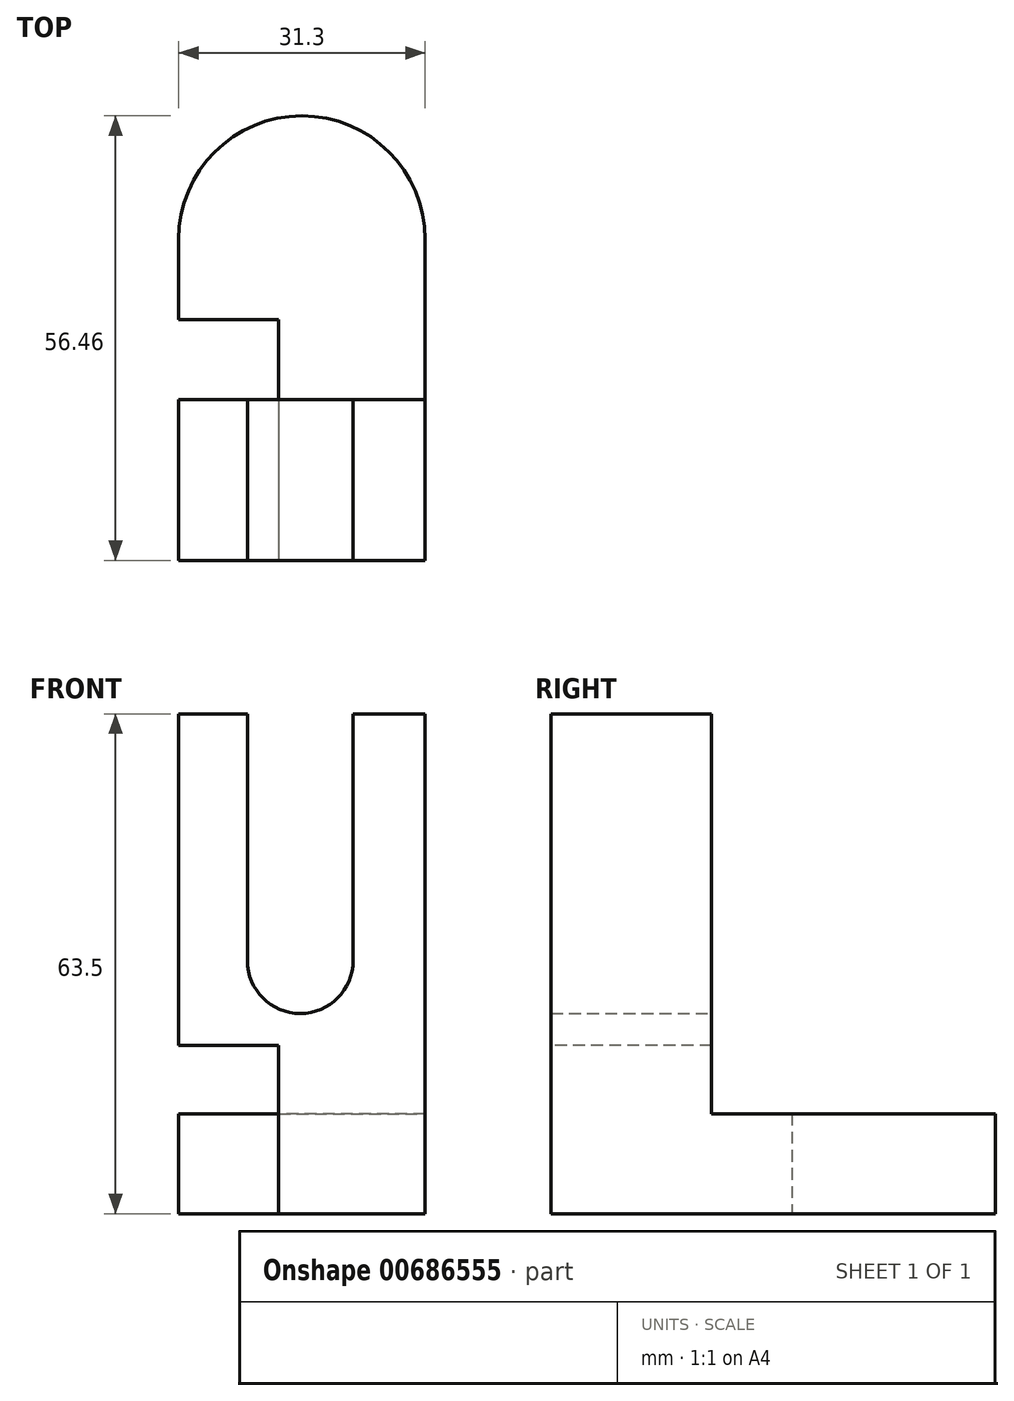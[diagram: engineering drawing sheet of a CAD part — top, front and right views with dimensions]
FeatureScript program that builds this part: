
annotation { "Feature Type Name" : "Feature", "Feature Type Description" : "" }
export const myFeature = defineFeature(function(context is Context, id is Id, definition is map)
    precondition{}
    {
        {
            var Q0;
            Q0=qCreatedBy(makeId("Top.planeOp"),FACE);
            var sketch = newSketch(context, id + "F0", { "sketchPlane" : qUnion([Q0])});
            skLineSegment(sketch, "E0.top", {"start": v(15.65, -20.4) * mm, "end": v(-15.65, -20.4) * mm});
            skLineSegment(sketch, "E0.left", {"start": v(15.65, 20.4) * mm, "end": v(15.65, -20.4) * mm});
            skLineSegment(sketch, "E0.right", {"start": v(-15.65, 20.4) * mm, "end": v(-15.65, -20.4) * mm});
            skPoint(sketch, "E0.middle", {"position": v(0, 0) * mm});
            skArc(sketch, "E1", {"start": v(15.65, 20.4) * mm, "mid": v(0, 36.06) * mm, "end": v(-15.65, 20.4) * mm});
            skSolve(sketch);
        }
        {
            var Q0;
            Q0=makeQuery(id+"F0.imprint","IMPRINT",FACE,{"disambiguationData":[TD([[makeQuery(id+"F0.imprint","IMPRINT",EDGE,{"derivedFrom":sQuery(id+"F0.wireOp",EDGE,"E0.top")}),-1.0]])]});
            extrude(context, id + "F1", {"entities" : qUnion([Q0]), "depth" : 12.7 * mm, "offsetDistance" : 25.4 * mm});
        }
        {
            var Q0;
            Q0=makeQuery(id+"F1.opExtrude","CAP_FACE",FACE,{"disambiguationData":[OSD([sQuery(id+"F0.wireOp",EDGE,"E0.top"),sQuery(id+"F0.wireOp",EDGE,"E0.left"),sQuery(id+"F0.wireOp",EDGE,"E0.right"),sQuery(id+"F0.wireOp",EDGE,"E1")])],"isStart":false});
            var sketch = newSketch(context, id + "F2", { "sketchPlane" : qUnion([Q0])});
            skLineSegment(sketch, "E2", {"start": v(-15.65, 0) * mm, "end": v(15.65, 0) * mm});
            skLineSegment(sketch, "E3", {"start": v(15.65, 0) * mm, "end": v(15.65, -20.4) * mm});
            skLineSegment(sketch, "E4", {"start": v(15.65, -20.4) * mm, "end": v(-15.65, -20.4) * mm});
            skLineSegment(sketch, "E5", {"start": v(-15.65, -20.4) * mm, "end": v(-15.65, 0) * mm});
            skSolve(sketch);
        }
        {
            var Q0;
            Q0=makeQuery(id+"F2.imprint","IMPRINT",FACE,{"disambiguationData":[TD([[makeQuery(id+"F2.imprint","IMPRINT",EDGE,{"derivedFrom":sQuery(id+"F2.wireOp",EDGE,"E2")}),-1.0]])]});
            extrude(context, id + "F3", {"entities" : qUnion([Q0]), "operationType" : NewBodyOperationType.ADD, "depth" : 50.8 * mm, "offsetDistance" : 25.4 * mm});
        }
        {
            var Q0;
            Q0=makeQuery(id+"F3.opExtrude","SWEPT_FACE",FACE,{"disambiguationData":[OSD([sQuery(id+"F2.wireOp",EDGE,"E2")])]});
            var sketch = newSketch(context, id + "F4", { "sketchPlane" : qUnion([Q0])});
            skLineSegment(sketch, "E6.bottom", {"start": v(-6.51, 63.5) * mm, "end": v(6.92, 63.5) * mm});
            skLineSegment(sketch, "E6.left", {"start": v(-6.51, 63.5) * mm, "end": v(-6.51, 32.15) * mm});
            skLineSegment(sketch, "E6.right", {"start": v(6.92, 63.5) * mm, "end": v(6.92, 32.15) * mm});
            skArc(sketch, "E7", {"start": v(-6.51, 32.15) * mm, "mid": v(0.2, 25.43) * mm, "end": v(6.92, 32.15) * mm});
            skSolve(sketch);
        }
        {
            var Q0;
            Q0=makeQuery(id+"F4.imprint","IMPRINT",FACE,{"disambiguationData":[TD([[makeQuery(id+"F4.imprint","IMPRINT",EDGE,{"derivedFrom":sQuery(id+"F4.wireOp",EDGE,"E6.bottom")}),1.0]])]});
            extrude(context, id + "F5", {"entities" : qUnion([Q0]), "operationType" : NewBodyOperationType.REMOVE, "oppositeDirection" : true, "depth" : 25.4 * mm, "offsetDistance" : 25.4 * mm});
        }
        {
            var Q0;
            Q0=makeQuery(id+"F3.boolean.opBoolean","MERGE",FACE,{"derivedFrom":[makeQuery(id+"F1.opExtrude","SWEPT_FACE",FACE,{"disambiguationData":[OSD([sQuery(id+"F0.wireOp",EDGE,"E0.right")])]}),makeQuery(id+"F3.opExtrude","SWEPT_FACE",FACE,{"disambiguationData":[OSD([sQuery(id+"F2.wireOp",EDGE,"E5")])]})]});
            var sketch = newSketch(context, id + "F6", { "sketchPlane" : qUnion([Q0])});
            skLineSegment(sketch, "E8", {"start": v(-10.2, 12.7) * mm, "end": v(-10.2, 0) * mm});
            skLineSegment(sketch, "E9", {"start": v(-10.2, 0) * mm, "end": v(20.4, 0) * mm});
            skLineSegment(sketch, "E10", {"start": v(20.4, 0) * mm, "end": v(20.4, 12.7) * mm});
            skLineSegment(sketch, "E11", {"start": v(0, 12.7) * mm, "end": v(-10.2, 12.7) * mm});
            skLineSegment(sketch, "E12", {"start": v(0, 12.7) * mm, "end": v(0, 21.4) * mm});
            skLineSegment(sketch, "E13", {"start": v(0, 21.4) * mm, "end": v(20.4, 21.4) * mm});
            skLineSegment(sketch, "E14", {"start": v(20.4, 21.4) * mm, "end": v(20.4, 12.7) * mm});
            skSolve(sketch);
        }
        {
            var Q0;
            {var subQ5=sQuery(id+"F6.wireOp",EDGE,"E8");Q0=makeQuery(id+"F6.imprint","IMPRINT",FACE,{"disambiguationData":[TD([[makeQuery(id+"F6.imprint","IMPRINT",EDGE,{"derivedFrom":subQ5}),1.0]])]});}
            extrude(context, id + "F7", {"entities" : qUnion([Q0]), "operationType" : NewBodyOperationType.REMOVE, "oppositeDirection" : true, "depth" : 12.7 * mm, "offsetDistance" : 25.4 * mm});
        }
    });
